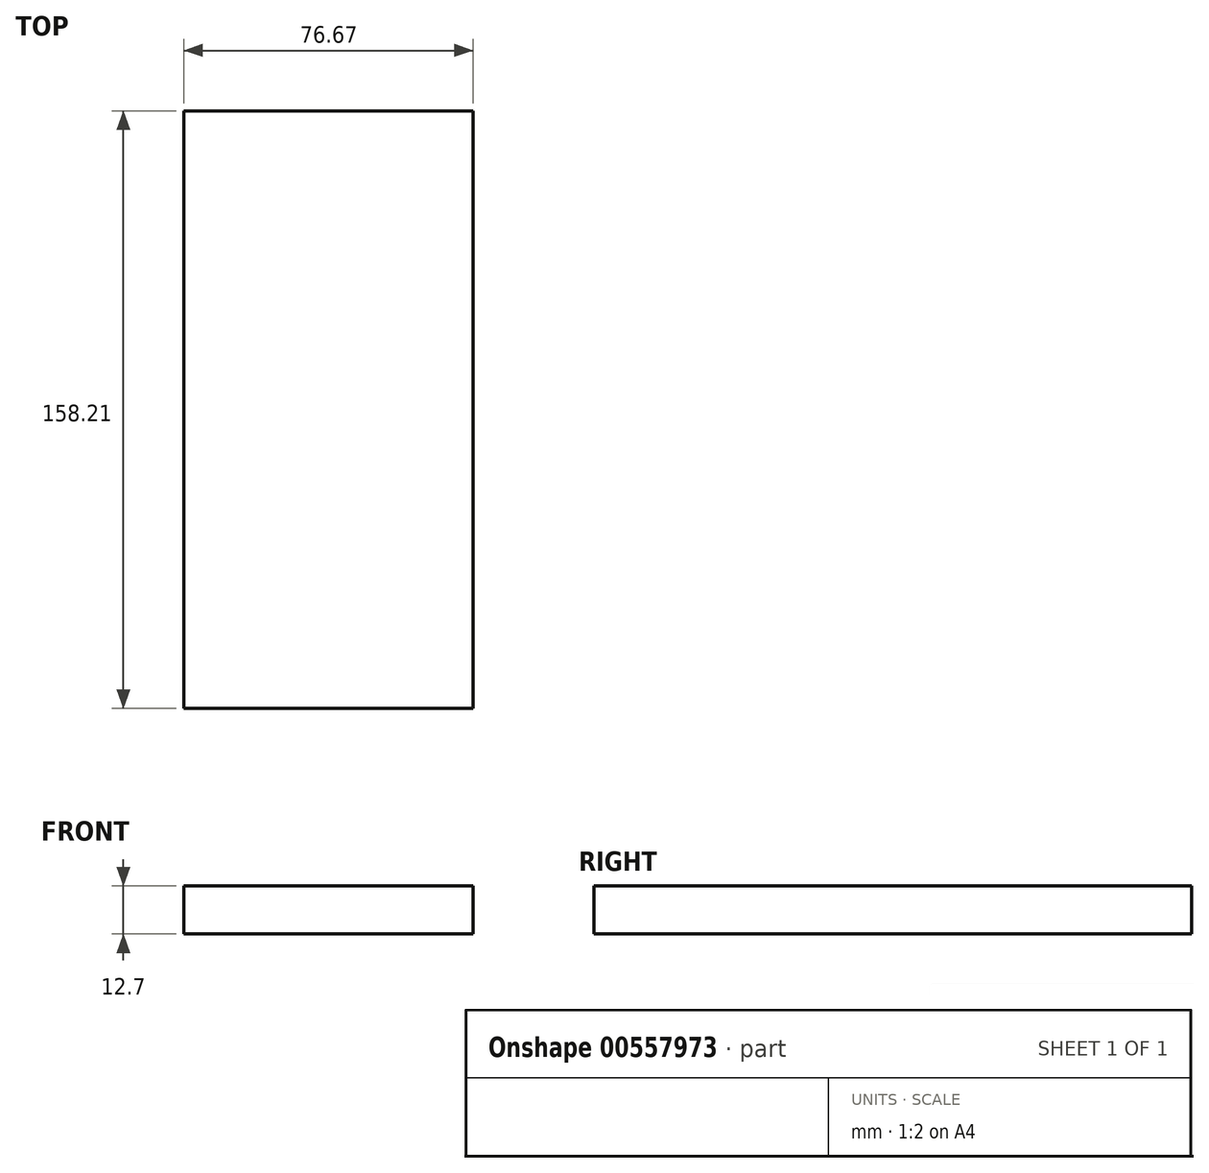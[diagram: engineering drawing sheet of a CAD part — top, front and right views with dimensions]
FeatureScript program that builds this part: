
annotation { "Feature Type Name" : "Feature", "Feature Type Description" : "" }
export const myFeature = defineFeature(function(context is Context, id is Id, definition is map)
    precondition{}
    {
        {
            var Q0;
            Q0=qCreatedBy(makeId("Top.planeOp"),FACE);
            var sketch = newSketch(context, id + "F0", { "sketchPlane" : qUnion([Q0])});
            skLineSegment(sketch, "E0.bottom", {"start": v(0, 0) * mm, "end": v(-76.67, 0) * mm});
            skLineSegment(sketch, "E0.top", {"start": v(0, 158.21) * mm, "end": v(-76.67, 158.21) * mm});
            skLineSegment(sketch, "E0.left", {"start": v(0, 0) * mm, "end": v(0, 158.21) * mm});
            skLineSegment(sketch, "E0.right", {"start": v(-76.67, 0) * mm, "end": v(-76.67, 158.21) * mm});
            skSolve(sketch);
        }
        {
            var Q0;
            Q0=makeQuery(id+"F0.imprint","IMPRINT",FACE,{"disambiguationData":[TD([[makeQuery(id+"F0.imprint","IMPRINT",EDGE,{"derivedFrom":sQuery(id+"F0.wireOp",EDGE,"E0.bottom")}),-1.0]])]});
            extrude(context, id + "F1", {"entities" : qUnion([Q0]), "depth" : 12.7 * mm, "offsetDistance" : 25.4 * mm});
        }
        {
            var Q0;
            Q0=makeQuery(id+"F1.opExtrude","CAP_FACE",FACE,{"disambiguationData":[OSD([sQuery(id+"F0.wireOp",EDGE,"E0.bottom"),sQuery(id+"F0.wireOp",EDGE,"E0.top"),sQuery(id+"F0.wireOp",EDGE,"E0.left"),sQuery(id+"F0.wireOp",EDGE,"E0.right")])],"isStart":false});
            var sketch = newSketch(context, id + "F2", { "sketchPlane" : qUnion([Q0])});
            skLineSegment(sketch, "E1.bottom", {"start": v(0, 0) * mm, "end": v(0, 0) * mm});
            skLineSegment(sketch, "E1.top", {"start": v(0, 158.21) * mm, "end": v(0, 158.21) * mm});
            skLineSegment(sketch, "E1.left", {"start": v(0, 0) * mm, "end": v(0, 158.21) * mm});
            skLineSegment(sketch, "E1.right", {"start": v(0, 0) * mm, "end": v(0, 158.21) * mm});
            skSolve(sketch);
        }
        {
            var Q0;
            Q0=sQuery(id+"F2.wireOp",EDGE,"E1.right");
            extrude(context, id + "F3", {"bodyType" : ToolBodyType.SURFACE, "surfaceEntities" : qUnion([Q0]), "depth" : 25.4 * mm, "offsetDistance" : 25.4 * mm});
        }
        {
            var Q0;
            Q0=makeQuery(id+"F1.opExtrude","CAP_FACE",FACE,{"disambiguationData":[OSD([sQuery(id+"F0.wireOp",EDGE,"E0.bottom"),sQuery(id+"F0.wireOp",EDGE,"E0.top"),sQuery(id+"F0.wireOp",EDGE,"E0.left"),sQuery(id+"F0.wireOp",EDGE,"E0.right")])],"isStart":false});
            var sketch = newSketch(context, id + "F4", { "sketchPlane" : qUnion([Q0])});
            skLineSegment(sketch, "E2.bottom", {"start": v(-76.67, 0) * mm, "end": v(0, 0) * mm});
            skLineSegment(sketch, "E2.top", {"start": v(-76.67, 0) * mm, "end": v(0, 0) * mm});
            skLineSegment(sketch, "E2.left", {"start": v(-76.67, 0) * mm, "end": v(-76.67, 0) * mm});
            skLineSegment(sketch, "E2.right", {"start": v(0, 0) * mm, "end": v(0, 0) * mm});
            skSolve(sketch);
        }
        {
            var Q0;
            Q0=sQuery(id+"F4.wireOp",EDGE,"E2.top");
            extrude(context, id + "F5", {"bodyType" : ToolBodyType.SURFACE, "surfaceEntities" : qUnion([Q0]), "depth" : 25.4 * mm, "offsetDistance" : 25.4 * mm});
        }
        {
            var Q0;
            Q0=makeQuery(id+"F1.opExtrude","CAP_FACE",FACE,{"disambiguationData":[OSD([sQuery(id+"F0.wireOp",EDGE,"E0.bottom"),sQuery(id+"F0.wireOp",EDGE,"E0.top"),sQuery(id+"F0.wireOp",EDGE,"E0.left"),sQuery(id+"F0.wireOp",EDGE,"E0.right")])],"isStart":false});
            var sketch = newSketch(context, id + "F6", { "sketchPlane" : qUnion([Q0])});
            skLineSegment(sketch, "E3.bottom", {"start": v(-76.67, 158.21) * mm, "end": v(-76.67, 158.21) * mm});
            skLineSegment(sketch, "E3.top", {"start": v(-76.67, 0) * mm, "end": v(-76.67, 0) * mm});
            skLineSegment(sketch, "E3.left", {"start": v(-76.67, 158.21) * mm, "end": v(-76.67, 0) * mm});
            skLineSegment(sketch, "E3.right", {"start": v(-76.67, 158.21) * mm, "end": v(-76.67, 0) * mm});
            skSolve(sketch);
        }
        {
            var Q0;
            Q0=sQuery(id+"F6.wireOp",EDGE,"E3.left");
            extrude(context, id + "F7", {"bodyType" : ToolBodyType.SURFACE, "surfaceEntities" : qUnion([Q0]), "depth" : 25.4 * mm, "offsetDistance" : 25.4 * mm});
        }
        {
            var Q0;
            Q0=makeQuery(id+"F1.opExtrude","CAP_FACE",FACE,{"disambiguationData":[OSD([sQuery(id+"F0.wireOp",EDGE,"E0.bottom"),sQuery(id+"F0.wireOp",EDGE,"E0.top"),sQuery(id+"F0.wireOp",EDGE,"E0.left"),sQuery(id+"F0.wireOp",EDGE,"E0.right")])],"isStart":false});
            var sketch = newSketch(context, id + "F8", { "sketchPlane" : qUnion([Q0])});
            skLineSegment(sketch, "E4.bottom", {"start": v(-76.67, 158.21) * mm, "end": v(0, 158.21) * mm});
            skLineSegment(sketch, "E4.top", {"start": v(-76.67, 158.21) * mm, "end": v(0, 158.21) * mm});
            skLineSegment(sketch, "E4.left", {"start": v(-76.67, 158.21) * mm, "end": v(-76.67, 158.21) * mm});
            skLineSegment(sketch, "E4.right", {"start": v(0, 158.21) * mm, "end": v(0, 158.21) * mm});
            skSolve(sketch);
        }
        {
            var Q0;
            Q0=sQuery(id+"F8.wireOp",EDGE,"E4.bottom");
            extrude(context, id + "F9", {"bodyType" : ToolBodyType.SURFACE, "surfaceEntities" : qUnion([Q0]), "depth" : 25.4 * mm, "offsetDistance" : 25.4 * mm});
        }
    });
